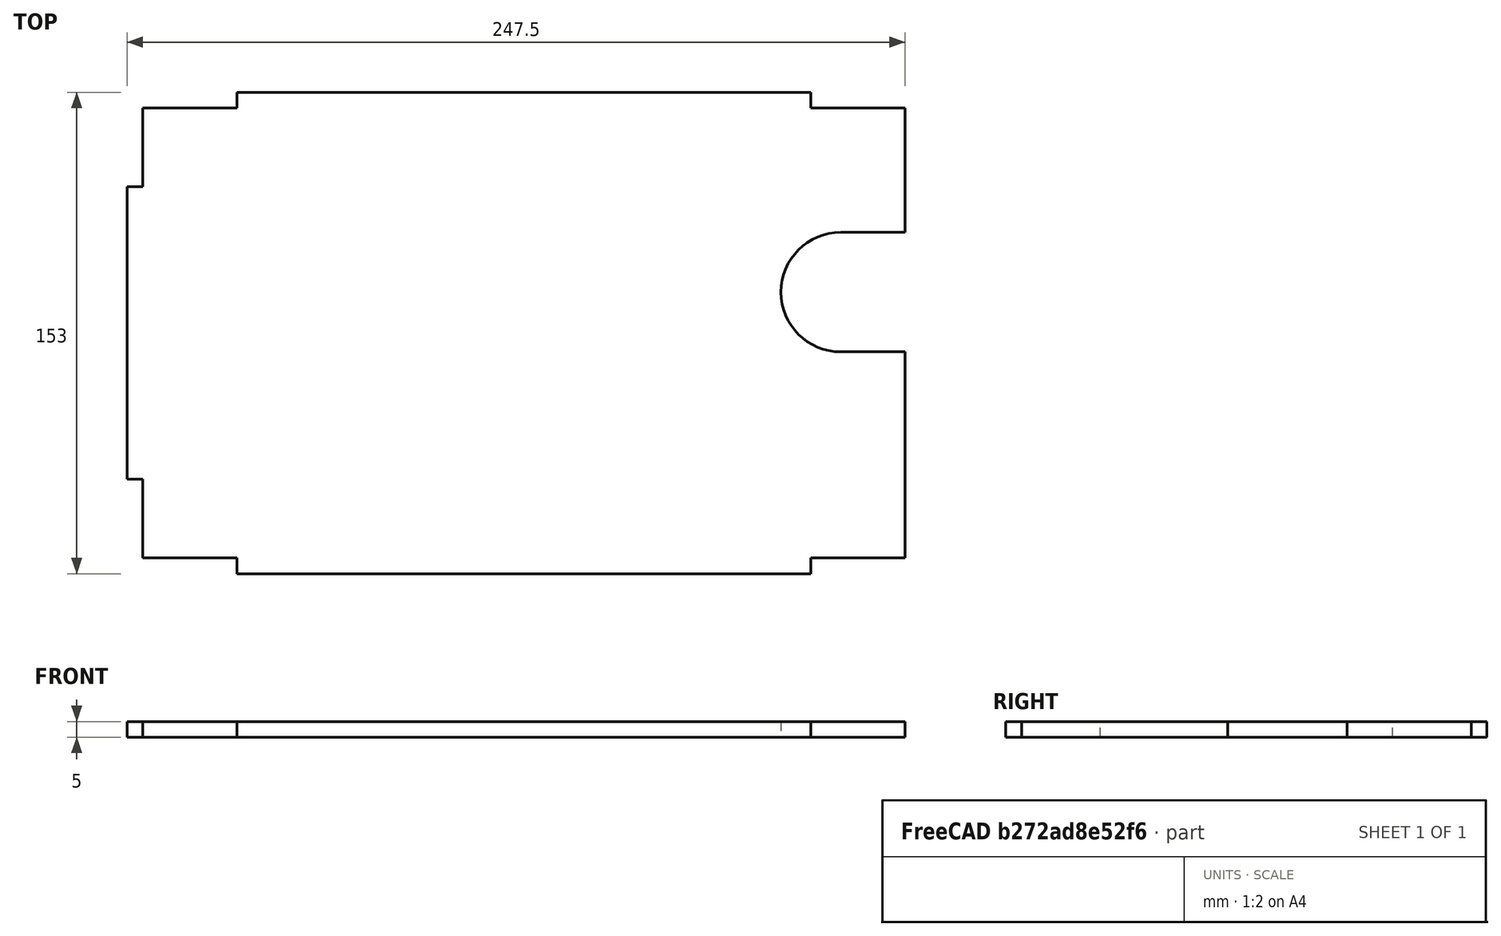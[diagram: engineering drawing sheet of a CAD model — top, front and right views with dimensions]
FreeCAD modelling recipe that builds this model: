
FCSTD DOCUMENT  (FreeCAD 0.15R4671 (Git))
Label: lower_side_axis_A
License: All rights reserved
LicenseURL: http://en.wikipedia.org/wiki/All_rights_reserved
objects: Sketcher::SketchObject×1, PartDesign::Pad×1
note: 3 computed .brp shape members not serialized (recipe doc carries the construction recipe); baked Part::Feature solids carry a one-line shape summary decoded from their .brp

FEATURE [Sketcher::SketchObject] Sketch
  sketch-geometry (20):
    g0: LineSegment StartX=91.25 StartY=76.5 StartZ=0 EndX=-91.25 EndY=76.5 EndZ=0
    g1: LineSegment StartX=-91.25 StartY=76.5 StartZ=0 EndX=-91.25 EndY=71.5 EndZ=0
    g2: LineSegment StartX=-91.25 StartY=71.5 StartZ=0 EndX=-121.25 EndY=71.5 EndZ=0
    g3: LineSegment StartX=-121.25 StartY=71.5 StartZ=0 EndX=-121.25 EndY=46.5 EndZ=0
    g4: LineSegment StartX=-121.25 StartY=46.5 StartZ=0 EndX=-126.25 EndY=46.5 EndZ=0
    g5: LineSegment StartX=-126.25 StartY=46.5 StartZ=0 EndX=-126.25 EndY=-46.5 EndZ=0
    g6: LineSegment StartX=-126.25 StartY=-46.5 StartZ=0 EndX=-121.25 EndY=-46.5 EndZ=0
    g7: LineSegment StartX=-121.25 StartY=-46.5 StartZ=0 EndX=-121.25 EndY=-71.5 EndZ=0
    g8: LineSegment StartX=-121.25 StartY=-71.5 StartZ=0 EndX=-91.25 EndY=-71.5 EndZ=0
    g9: LineSegment StartX=-91.25 StartY=-71.5 StartZ=0 EndX=-91.25 EndY=-76.5 EndZ=0
    g10: LineSegment StartX=-91.25 StartY=-76.5 StartZ=0 EndX=91.25 EndY=-76.5 EndZ=0
    g11: LineSegment StartX=91.25 StartY=-76.5 StartZ=0 EndX=91.25 EndY=-71.5 EndZ=0
    g12: LineSegment StartX=121.25 StartY=-71.5 StartZ=0 EndX=121.25 EndY=-6 EndZ=0
    g13: LineSegment StartX=121.25 StartY=32 StartZ=0 EndX=121.25 EndY=71.5 EndZ=0
    g14: LineSegment StartX=121.25 StartY=71.5 StartZ=0 EndX=91.25 EndY=71.5 EndZ=0
    g15: LineSegment StartX=91.25 StartY=71.5 StartZ=0 EndX=91.25 EndY=76.5 EndZ=0
    g16: LineSegment StartX=121.25 StartY=32 StartZ=0 EndX=100.75 EndY=32 EndZ=0
    g17: ArcOfCircle CenterX=100.75 CenterY=13 CenterZ=0 NormalX=0 NormalY=0 NormalZ=1 Radius=19 StartAngle=1.5708 EndAngle=4.71239
    g18: LineSegment StartX=100.75 StartY=-6 StartZ=0 EndX=121.25 EndY=-6 EndZ=0
    g19: LineSegment StartX=91.25 StartY=-71.5 StartZ=0 EndX=121.25 EndY=-71.5 EndZ=0
  constraints (59):
    c: Coincident(g2,g3)
    c: Coincident(g1,g2)
    c: Coincident(g0,g1)
    c: Coincident(g0,g15)
    c: Coincident(g14,g15)
    c: Coincident(g13,g14)
    c: Coincident(g10,g11)
    c: Coincident(g9,g10)
    c: Coincident(g8,g9)
    c: Coincident(g7,g8)
    c: Coincident(g6,g7)
    c: Coincident(g5,g6)
    c: Coincident(g4,g5)
    c: Vertical(g5)
    c: Vertical(g3)
    c: Vertical(g1)
    c: Vertical(g15)
    c: Vertical(g13)
    c: Vertical(g12)
    c: Vertical(g11)
    c: Vertical(g9)
    c: Vertical(g7)
    c: Horizontal(g6)
    c: Horizontal(g8)
    c: Horizontal(g10)
    c: Horizontal(g14)
    c: Horizontal(g0)
    c: Horizontal(g2)
    c: Horizontal(g4)
    c: Equal(g3,g7)
    c: Equal(g4,g6)
    c: Equal(g6,g9)
    c: Equal(g9,g11)
    c: Equal(g11,g15)
    c: Equal(g15,g1)
    c: Coincident(g3,g4)
    c: DistanceY(g1) = -5
    c: DistanceY(g1,g8) = -143
    c: DistanceX(g2,g13) = 242.5
    c: Coincident(g13,g16)
    c: Horizontal(g16)
    c: Tangent(g16,g17) = -1.5708
    c: Tangent(g17,g18) = -1.5708
    c: Horizontal(g18)
    c: DistanceY(g17,g14) = 58.5
    c: DistanceX(g17,g14) = -9.5
    c: Coincident(g12,g18)
    c: Radius(g17) = 19
    c: Equal(g16,g18)
    c: Coincident(g19,g11)
    c: Coincident(g19,g12)
    c: Horizontal(g19)
    c: Equal(g19,g14)
    c: Equal(g14,g2)
    c: Equal(g2,g8)
    c: DistanceX(g0) = -182.5
    c: DistanceY(g5) = -93
    c: Symmetric(g10,g0,g-1)
    c: Symmetric(g9,g10,g-2)
FEATURE [PartDesign::Pad] Pad
  Length = 5
  Length2 = 100
  Midplane = true
  Sketch = -> Sketch
  Type = 0
